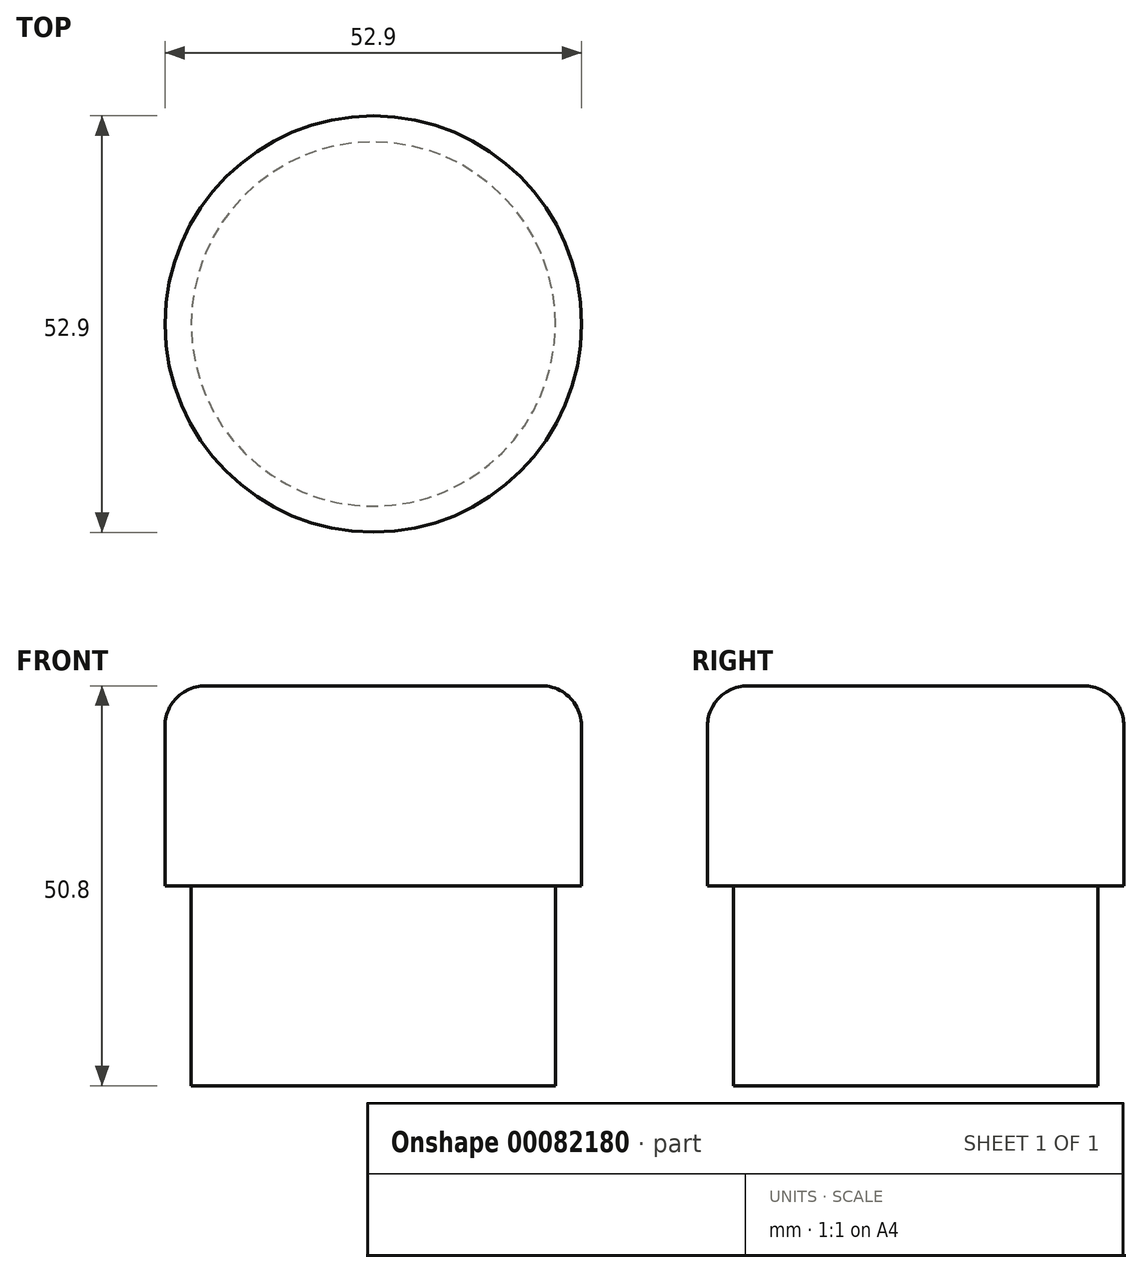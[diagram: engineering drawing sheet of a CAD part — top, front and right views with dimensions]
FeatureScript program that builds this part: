
annotation { "Feature Type Name" : "Feature", "Feature Type Description" : "" }
export const myFeature = defineFeature(function(context is Context, id is Id, definition is map)
    precondition{}
    {
        {
            var Q0;
            Q0=qCreatedBy(makeId("Top.planeOp"),FACE);
            var sketch = newSketch(context, id + "F0", { "sketchPlane" : qUnion([Q0])});
            skCircle(sketch, "E0", {"center": v(0, 0) * mm, "radius": 23.14 * mm});
            skSolve(sketch);
        }
        {
            var Q0;
            Q0 = qSketchRegion(id + "F0", true);
            extrude(context, id + "F1", {"entities" : qUnion([Q0]), "depth" : 25.4 * mm});
        }
        {
            var Q0;
            Q0=makeQuery(id+"F1.opExtrude","CAP_FACE",FACE,{"disambiguationData":[OSD([sQuery(id+"F0.wireOp",EDGE,"E0")])],"isStart":false});
            var sketch = newSketch(context, id + "F2", { "sketchPlane" : qUnion([Q0])});
            skCircle(sketch, "E1", {"center": v(0, 0) * mm, "radius": 26.45 * mm});
            skSolve(sketch);
        }
        {
            var Q0;
            Q0=makeQuery(id+"F2.imprint","IMPRINT",FACE,{"disambiguationData":[TD([[makeQuery(id+"F2.imprint","IMPRINT",EDGE,{"derivedFrom":sQuery(id+"F2.wireOp",EDGE,"E1")}),1.0]])]});
            var Q1;
            Q1=makeQuery(id+"F1.opExtrude","CAP_FACE",FACE,{"disambiguationData":[OSD([sQuery(id+"F0.wireOp",EDGE,"E0")])],"isStart":false});
            var Q2;
            Q2=makeQuery(id+"F2.imprint","IMPRINT",FACE,{"disambiguationData":[TD([[makeQuery(id+"F2.imprint","IMPRINT",EDGE,{"derivedFrom":makeQuery(id+"F1.opExtrude","CAP_EDGE",EDGE,{"disambiguationData":[OSD([sQuery(id+"F0.wireOp",EDGE,"E0")])],"isStart":false})}),1.0]])]});
            extrude(context, id + "F3", {"entities" : qUnion([Q0, Q1, Q2]), "operationType" : NewBodyOperationType.ADD, "depth" : 25.4 * mm});
        }
        {
            var Q0;
            Q0=makeQuery(id+"F3.opExtrude","CAP_EDGE",EDGE,{"disambiguationData":[OSD([sQuery(id+"F2.wireOp",EDGE,"E1")])],"isStart":false});
            fillet(context, id + "F4", {"entities" : qUnion([Q0]), "radius" : 5.08 * mm, "tangentPropagation" : true, "allowEdgeOverflow" : false});
        }
    });
